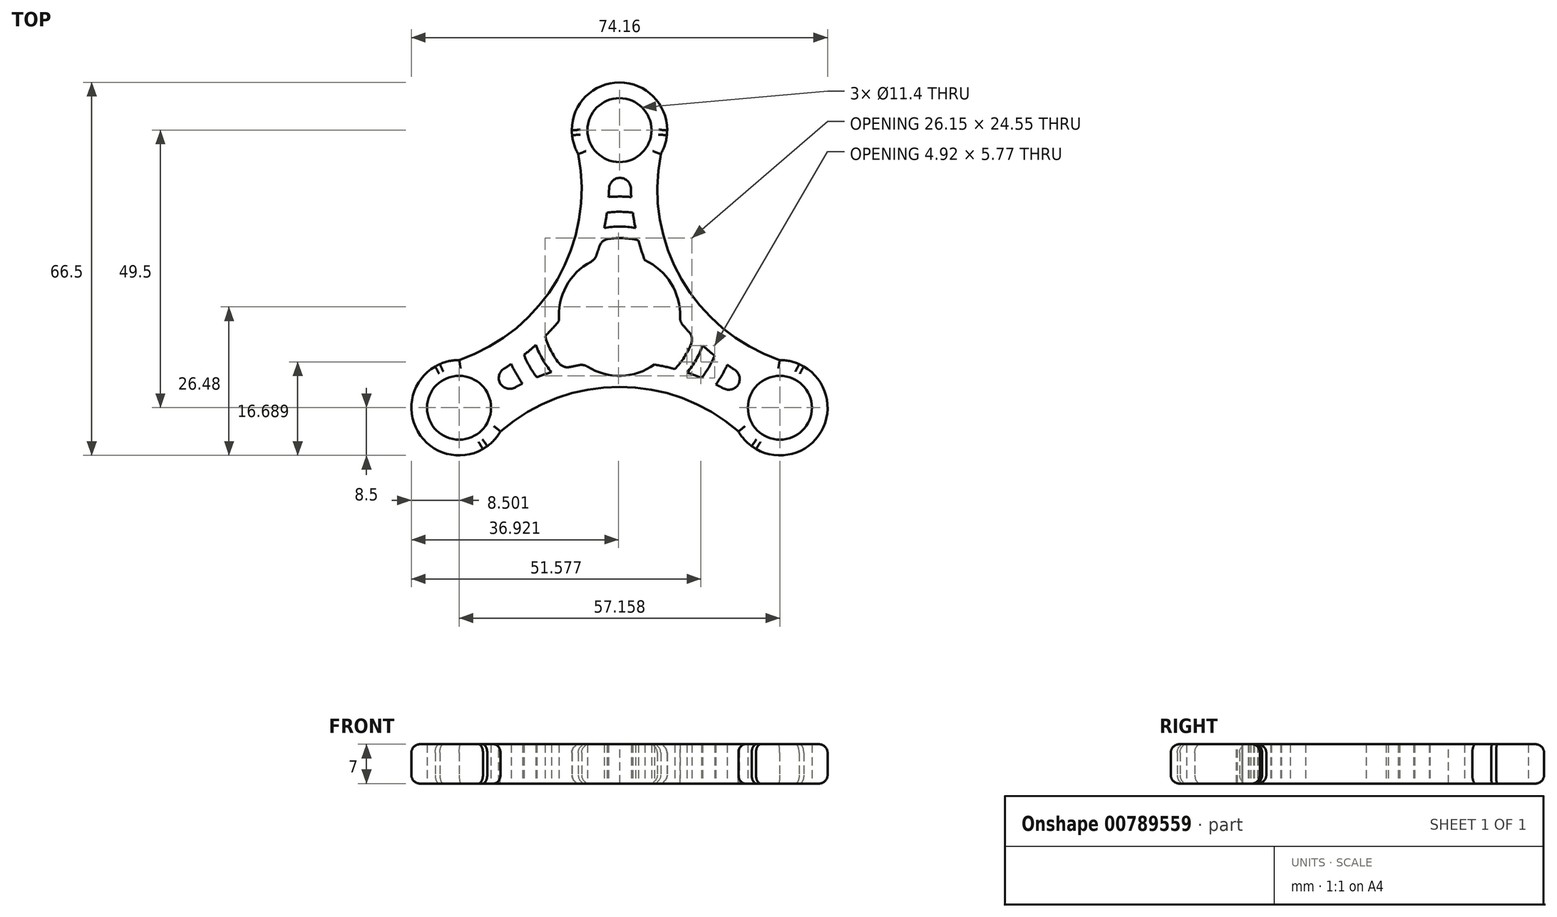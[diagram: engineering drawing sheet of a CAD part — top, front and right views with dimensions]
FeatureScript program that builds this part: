
annotation { "Feature Type Name" : "Feature", "Feature Type Description" : "" }
export const myFeature = defineFeature(function(context is Context, id is Id, definition is map)
    precondition{}
    {
        {
            var Q0;
            Q0=qCreatedBy(makeId("Top.planeOp"),FACE);
            var sketch = newSketch(context, id + "F0", { "sketchPlane" : qUnion([Q0])});
            skCircle(sketch, "E0", {"center": v(0, 0) * mm, "radius": 10.8 * mm});
            skCircle(sketch, "E1", {"center": v(0, 33) * mm, "radius": 5.7 * mm});
            skArc(sketch, "E2", {"start": v(7.35, 28.73) * mm, "mid": v(0, 41.5) * mm, "end": v(-7.35, 28.73) * mm});
            skCircle(sketch, "E3.1.0", {"center": v(-28.58, -16.5) * mm, "radius": 5.7 * mm});
            skArc(sketch, "E3.1.1", {"start": v(-28.55, -8) * mm, "mid": v(-35.94, -20.75) * mm, "end": v(-21.2, -20.73) * mm});
            skCircle(sketch, "E3.2.0", {"center": v(28.58, -16.5) * mm, "radius": 5.7 * mm});
            skArc(sketch, "E3.2.1", {"start": v(22.31, -10.76) * mm, "mid": v(21.17, -12.34) * mm, "end": v(20.41, -14.14) * mm});
            skLineSegment(sketch, "E4", {"start": v(0, 0) * mm, "end": v(28.58, -16.5) * mm, "construction": true});
            skLineSegment(sketch, "E5", {"start": v(28.58, -16.5) * mm, "end": v(38.1, 0) * mm, "construction": true});
            skArc(sketch, "E6", {"start": v(8.5, 33) * mm, "mid": v(8.47, 32.54) * mm, "end": v(8.45, 32.09) * mm});
            skArc(sketch, "E7.1.0", {"start": v(-32.83, -9.14) * mm, "mid": v(-32.42, -8.93) * mm, "end": v(-32.01, -8.72) * mm});
            skArc(sketch, "E7.2.0", {"start": v(24.33, -23.86) * mm, "mid": v(23.95, -23.6) * mm, "end": v(23.56, -23.36) * mm});
            skArc(sketch, "E8", {"start": v(2.04, 24.75) * mm, "mid": v(2.03, 22.9) * mm, "end": v(2.1, 21.05) * mm});
            skArc(sketch, "E9.trimOffspring", {"start": v(10.74, -1.1) * mm, "mid": v(11.94, -2.5) * mm, "end": v(13.2, -3.85) * mm});
            skArc(sketch, "E10.trimOffspring", {"start": v(-6.32, -8.76) * mm, "mid": v(-8.14, -9.1) * mm, "end": v(-9.94, -9.5) * mm});
            skArc(sketch, "E11.trimOffspring", {"start": v(-4.43, 9.85) * mm, "mid": v(-3.8, 11.6) * mm, "end": v(-3.27, 13.36) * mm});
            skArc(sketch, "E12.trimOffspring", {"start": v(32.01, -8.72) * mm, "mid": v(32.42, -8.93) * mm, "end": v(32.83, -9.14) * mm});
            skArc(sketch, "E13.trimOffspring", {"start": v(-23.56, -23.36) * mm, "mid": v(-23.95, -23.6) * mm, "end": v(-24.33, -23.86) * mm});
            skArc(sketch, "E14.trimOffspring", {"start": v(-8.45, 32.09) * mm, "mid": v(-8.47, 32.54) * mm, "end": v(-8.5, 33) * mm});
            skArc(sketch, "E15", {"start": v(7.35, 28.73) * mm, "mid": v(11.06, 6.38) * mm, "end": v(28.55, -8) * mm});
            skArc(sketch, "E16.1.0", {"start": v(-28.55, -8) * mm, "mid": v(-11.06, 6.38) * mm, "end": v(-7.35, 28.73) * mm});
            skArc(sketch, "E16.2.0", {"start": v(21.2, -20.73) * mm, "mid": v(0, -12.77) * mm, "end": v(-21.2, -20.73) * mm});
            skPoint(sketch, "E17.orphan", {"position": v(-2.9, 33) * mm});
            skPoint(sketch, "E18.orphan", {"position": v(3.18, 33) * mm});
            skArc(sketch, "E19.trimOffspring", {"start": v(-1.84, 24.7) * mm, "mid": v(0.1, 24.5) * mm, "end": v(2.04, 24.75) * mm});
            skPoint(sketch, "E20.orphan", {"position": v(-8.5, 33) * mm});
            skArc(sketch, "E21.trimOffspring", {"start": v(20.41, -14.14) * mm, "mid": v(18.82, -13.2) * mm, "end": v(17.18, -12.35) * mm});
            skArc(sketch, "E22.trimOffspring", {"start": v(21.2, -20.73) * mm, "mid": v(35.94, -20.75) * mm, "end": v(28.55, -8) * mm});
            skPoint(sketch, "E23.orphan", {"position": v(24.33, -23.86) * mm});
            skArc(sketch, "E24.trimOffspring", {"start": v(-22.45, -10.6) * mm, "mid": v(-20.84, -9.7) * mm, "end": v(-19.28, -8.7) * mm});
            skArc(sketch, "E25.trimOffspring", {"start": v(-20.47, -13.94) * mm, "mid": v(-21.27, -12.16) * mm, "end": v(-22.45, -10.6) * mm});
            skPoint(sketch, "E26.orphan", {"position": v(-32.83, -9.14) * mm});
            skPoint(sketch, "E27.orphan", {"position": v(-24.33, -23.86) * mm});
            skArc(sketch, "E28", {"start": v(-19.28, -8.7) * mm, "mid": v(-18.36, -10.5) * mm, "end": v(-17.28, -12.2) * mm});
            skArc(sketch, "E29", {"start": v(-17.02, -7.08) * mm, "mid": v(-16, -9.15) * mm, "end": v(-14.73, -11.08) * mm});
            skArc(sketch, "E30", {"start": v(-13.24, -3.74) * mm, "mid": v(-11.94, -6.83) * mm, "end": v(-9.94, -9.5) * mm});
            skArc(sketch, "E31", {"start": v(-14.88, -5.3) * mm, "mid": v(-13.72, -7.84) * mm, "end": v(-12.12, -10.14) * mm});
            skArc(sketch, "E32.trimOffspring", {"start": v(9.86, -9.6) * mm, "mid": v(11.88, -6.93) * mm, "end": v(13.2, -3.85) * mm});
            skArc(sketch, "E33.trimOffspring", {"start": v(12.04, -10.24) * mm, "mid": v(13.65, -7.96) * mm, "end": v(14.84, -5.43) * mm});
            skArc(sketch, "E34.trimOffspring", {"start": v(14.64, -11.2) * mm, "mid": v(15.92, -9.28) * mm, "end": v(16.96, -7.22) * mm});
            skArc(sketch, "E35.trimOffspring", {"start": v(17.18, -12.35) * mm, "mid": v(18.28, -10.65) * mm, "end": v(19.21, -8.86) * mm});
            skArc(sketch, "E36.trimOffspring", {"start": v(-17.28, -12.2) * mm, "mid": v(-18.9, -13.04) * mm, "end": v(-20.47, -13.94) * mm});
            skArc(sketch, "E37.trimOffspring", {"start": v(-17.02, -7.08) * mm, "mid": v(-15.93, -6.21) * mm, "end": v(-14.88, -5.3) * mm});
            skArc(sketch, "E38.trimOffspring", {"start": v(-13.24, -3.74) * mm, "mid": v(-11.96, -2.4) * mm, "end": v(-10.75, -1) * mm});
            skArc(sketch, "E39.trimOffspring", {"start": v(-12.12, -10.14) * mm, "mid": v(-13.43, -10.58) * mm, "end": v(-14.73, -11.08) * mm});
            skArc(sketch, "E40.trimOffspring", {"start": v(2.1, 21.05) * mm, "mid": v(0.09, 21.16) * mm, "end": v(-1.93, 21.07) * mm});
            skArc(sketch, "E41.trimOffspring", {"start": v(2.38, 18.28) * mm, "mid": v(0.08, 18.43) * mm, "end": v(-2.23, 18.3) * mm});
            skArc(sketch, "E42.trimOffspring", {"start": v(2.85, 15.54) * mm, "mid": v(0.06, 15.8) * mm, "end": v(-2.72, 15.56) * mm});
            skArc(sketch, "E43.trimOffspring", {"start": v(3.38, 13.33) * mm, "mid": v(0.06, 13.75) * mm, "end": v(-3.27, 13.36) * mm});
            skArc(sketch, "E44.trimOffspring", {"start": v(14.84, -5.43) * mm, "mid": v(15.88, -6.34) * mm, "end": v(16.96, -7.22) * mm});
            skArc(sketch, "E45.trimOffspring", {"start": v(9.86, -9.6) * mm, "mid": v(8.06, -9.16) * mm, "end": v(6.25, -8.81) * mm});
            skArc(sketch, "E46.trimOffspring", {"start": v(14.64, -11.2) * mm, "mid": v(13.35, -10.7) * mm, "end": v(12.04, -10.24) * mm});
            skArc(sketch, "E47.trimOffspring", {"start": v(19.21, -8.86) * mm, "mid": v(20.74, -9.85) * mm, "end": v(22.31, -10.76) * mm});
            skArc(sketch, "E48.trimOffspring", {"start": v(3.38, 13.33) * mm, "mid": v(3.9, 11.56) * mm, "end": v(4.5, 9.81) * mm});
            skArc(sketch, "E49.trimOffspring", {"start": v(-2.72, 15.56) * mm, "mid": v(-2.45, 16.93) * mm, "end": v(-2.23, 18.3) * mm});
            skArc(sketch, "E50.trimOffspring", {"start": v(-1.93, 21.07) * mm, "mid": v(-1.84, 22.88) * mm, "end": v(-1.84, 24.7) * mm});
            skArc(sketch, "E51.trimOffspring", {"start": v(2.38, 18.28) * mm, "mid": v(2.59, 16.9) * mm, "end": v(2.85, 15.54) * mm});
            skSolve(sketch);
        }
        {
            var Q0;
            Q0=makeQuery(id+"F0.imprint","IMPRINT",FACE,{"disambiguationData":[TD([[makeQuery(id+"F0.imprint","IMPRINT",EDGE,{"derivedFrom":sQuery(id+"F0.wireOp",EDGE,"E1")}),-1.0]])]});
            extrude(context, id + "F1", {"entities" : qUnion([Q0]), "depth" : 7 * mm, "offsetDistance" : 25 * mm});
        }
        {
            var Q0;
            Q0=makeQuery(id+"F1.opExtrude","SWEPT_EDGE",EDGE,{"disambiguationData":[OSD([sQuery(id+"F0.wireOp",EDGE,"E11.trimOffspring"),sQuery(id+"F0.wireOp",EDGE,"E19.trimOffspring")])]});
            var Q1;
            Q1=makeQuery(id+"F1.opExtrude","SWEPT_EDGE",EDGE,{"disambiguationData":[OSD([sQuery(id+"F0.wireOp",EDGE,"E8"),sQuery(id+"F0.wireOp",EDGE,"E19.trimOffspring")])]});
            var Q2;
            Q2=makeQuery(id+"F1.opExtrude","SWEPT_EDGE",EDGE,{"disambiguationData":[OSD([sQuery(id+"F0.wireOp",EDGE,"E3.2.1"),sQuery(id+"F0.wireOp",EDGE,"E9.trimOffspring")])]});
            var Q3;
            Q3=makeQuery(id+"F1.opExtrude","SWEPT_EDGE",EDGE,{"disambiguationData":[OSD([sQuery(id+"F0.wireOp",EDGE,"E3.2.1"),sQuery(id+"F0.wireOp",EDGE,"E21.trimOffspring")])]});
            var Q4;
            Q4=makeQuery(id+"F1.opExtrude","SWEPT_EDGE",EDGE,{"disambiguationData":[OSD([sQuery(id+"F0.wireOp",EDGE,"E10.trimOffspring"),sQuery(id+"F0.wireOp",EDGE,"E25.trimOffspring")])]});
            var Q5;
            Q5=makeQuery(id+"F1.opExtrude","SWEPT_EDGE",EDGE,{"disambiguationData":[OSD([sQuery(id+"F0.wireOp",EDGE,"E24.trimOffspring"),sQuery(id+"F0.wireOp",EDGE,"E25.trimOffspring")])]});
            fillet(context, id + "F2", {"entities" : qUnion([Q0, Q1, Q2, Q3, Q4, Q5]), "radius" : 2 * mm, "tangentPropagation" : true, "allowEdgeOverflow" : false});
        }
        {
            var Q0;
            Q0=makeQuery(id+"F1.opExtrude","CAP_EDGE",EDGE,{"disambiguationData":[OSD([sQuery(id+"F0.wireOp",EDGE,"E16.2.0")])],"isStart":false});
            var Q1;
            Q1=makeQuery(id+"F1.opExtrude","CAP_EDGE",EDGE,{"disambiguationData":[OSD([sQuery(id+"F0.wireOp",EDGE,"E15")])],"isStart":false});
            var Q2;
            Q2=makeQuery(id+"F1.opExtrude","CAP_EDGE",EDGE,{"disambiguationData":[OSD([sQuery(id+"F0.wireOp",EDGE,"E16.1.0")])],"isStart":false});
            var Q3;
            Q3=makeQuery(id+"F1.opExtrude","CAP_EDGE",EDGE,{"disambiguationData":[OSD([sQuery(id+"F0.wireOp",EDGE,"E16.2.0")])],"isStart":true});
            var Q4;
            Q4=makeQuery(id+"F1.opExtrude","CAP_EDGE",EDGE,{"disambiguationData":[OSD([sQuery(id+"F0.wireOp",EDGE,"E15")])],"isStart":true});
            var Q5;
            Q5=makeQuery(id+"F1.opExtrude","CAP_EDGE",EDGE,{"disambiguationData":[OSD([sQuery(id+"F0.wireOp",EDGE,"E16.1.0")])],"isStart":true});
            var Q6;
            {var subQ0=sQuery(id+"F0.wireOp",EDGE,"E3.1.1");Q6=makeQuery(id+"F1.opExtrude","CAP_EDGE",EDGE,{"disambiguationData":[OSD([subQ0]),TDD([makeQuery(id+"F0.imprint","IMPRINT",EDGE,{"disambiguationData":[TD([[makeQuery(id+"F0.imprint","INTERSECT",VERTEX,{"disambiguationData":[OD(0.0)],"derivedFrom":[subQ0,sQuery(id+"F0.wireOp",EDGE,"E7.1.0")]}),-1.0]])],"derivedFrom":subQ0})])],"isStart":true});}
            var Q7;
            {var subQ0=sQuery(id+"F0.wireOp",EDGE,"E3.1.1");Q7=makeQuery(id+"F1.opExtrude","CAP_EDGE",EDGE,{"disambiguationData":[OSD([subQ0]),TDD([makeQuery(id+"F0.imprint","IMPRINT",EDGE,{"disambiguationData":[TD([[makeQuery(id+"F0.imprint","INTERSECT",VERTEX,{"derivedFrom":[subQ0,sQuery(id+"F0.wireOp",EDGE,"E16.1.0")]}),-1.0]])],"derivedFrom":subQ0})])],"isStart":true});}
            var Q8;
            Q8=makeQuery(id+"F1.opExtrude","CAP_EDGE",EDGE,{"disambiguationData":[OSD([sQuery(id+"F0.wireOp",EDGE,"E7.1.0")])],"isStart":true});
            var Q9;
            {var subQ0=sQuery(id+"F0.wireOp",EDGE,"E3.1.1");Q9=makeQuery(id+"F1.opExtrude","CAP_EDGE",EDGE,{"disambiguationData":[OSD([subQ0]),TDD([makeQuery(id+"F0.imprint","IMPRINT",EDGE,{"disambiguationData":[TD([[makeQuery(id+"F0.imprint","INTERSECT",VERTEX,{"derivedFrom":[subQ0,sQuery(id+"F0.wireOp",EDGE,"E16.2.0")]}),1.0]])],"derivedFrom":subQ0})])],"isStart":true});}
            var Q10;
            Q10=makeQuery(id+"F1.opExtrude","CAP_EDGE",EDGE,{"disambiguationData":[OSD([sQuery(id+"F0.wireOp",EDGE,"E13.trimOffspring")])],"isStart":true});
            var Q11;
            {var subQ0=sQuery(id+"F0.wireOp",EDGE,"E22.trimOffspring");Q11=makeQuery(id+"F1.opExtrude","CAP_EDGE",EDGE,{"disambiguationData":[OSD([subQ0]),TDD([makeQuery(id+"F0.imprint","IMPRINT",EDGE,{"disambiguationData":[TD([[makeQuery(id+"F0.imprint","INTERSECT",VERTEX,{"disambiguationData":[OD(0.0)],"derivedFrom":[sQuery(id+"F0.wireOp",EDGE,"E12.trimOffspring"),subQ0]}),-1.0]])],"derivedFrom":subQ0})])],"isStart":true});}
            var Q12;
            Q12=makeQuery(id+"F1.opExtrude","CAP_EDGE",EDGE,{"disambiguationData":[OSD([sQuery(id+"F0.wireOp",EDGE,"E12.trimOffspring")])],"isStart":true});
            var Q13;
            {var subQ0=sQuery(id+"F0.wireOp",EDGE,"E22.trimOffspring");Q13=makeQuery(id+"F1.opExtrude","CAP_EDGE",EDGE,{"disambiguationData":[OSD([subQ0]),TDD([makeQuery(id+"F0.imprint","IMPRINT",EDGE,{"disambiguationData":[TD([[makeQuery(id+"F0.imprint","INTERSECT",VERTEX,{"disambiguationData":[OD(0.0)],"derivedFrom":[sQuery(id+"F0.wireOp",EDGE,"E7.2.0"),subQ0]}),-1.0]])],"derivedFrom":subQ0})])],"isStart":true});}
            var Q14;
            Q14=makeQuery(id+"F1.opExtrude","CAP_EDGE",EDGE,{"disambiguationData":[OSD([sQuery(id+"F0.wireOp",EDGE,"E7.2.0")])],"isStart":true});
            var Q15;
            {var subQ0=sQuery(id+"F0.wireOp",EDGE,"E22.trimOffspring");Q15=makeQuery(id+"F1.opExtrude","CAP_EDGE",EDGE,{"disambiguationData":[OSD([subQ0]),TDD([makeQuery(id+"F0.imprint","IMPRINT",EDGE,{"disambiguationData":[TD([[makeQuery(id+"F0.imprint","INTERSECT",VERTEX,{"disambiguationData":[OD(1.0)],"derivedFrom":[sQuery(id+"F0.wireOp",EDGE,"E7.2.0"),subQ0]}),1.0]])],"derivedFrom":subQ0})])],"isStart":true});}
            var Q16;
            {var subQ0=sQuery(id+"F0.wireOp",EDGE,"E2");Q16=makeQuery(id+"F1.opExtrude","CAP_EDGE",EDGE,{"disambiguationData":[OSD([subQ0]),TDD([makeQuery(id+"F0.imprint","IMPRINT",EDGE,{"disambiguationData":[TD([[makeQuery(id+"F0.imprint","INTERSECT",VERTEX,{"derivedFrom":[subQ0,sQuery(id+"F0.wireOp",EDGE,"E16.1.0")]}),1.0]])],"derivedFrom":subQ0})])],"isStart":true});}
            var Q17;
            Q17=makeQuery(id+"F1.opExtrude","CAP_EDGE",EDGE,{"disambiguationData":[OSD([sQuery(id+"F0.wireOp",EDGE,"E14.trimOffspring")])],"isStart":true});
            var Q18;
            {var subQ0=sQuery(id+"F0.wireOp",EDGE,"E2");Q18=makeQuery(id+"F1.opExtrude","CAP_EDGE",EDGE,{"disambiguationData":[OSD([subQ0]),TDD([makeQuery(id+"F0.imprint","IMPRINT",EDGE,{"disambiguationData":[TD([[makeQuery(id+"F0.imprint","INTERSECT",VERTEX,{"disambiguationData":[OD(0.0)],"derivedFrom":[subQ0,sQuery(id+"F0.wireOp",EDGE,"E6")]}),-1.0]])],"derivedFrom":subQ0})])],"isStart":true});}
            var Q19;
            {var subQ0=sQuery(id+"F0.wireOp",EDGE,"E2");Q19=makeQuery(id+"F1.opExtrude","CAP_EDGE",EDGE,{"disambiguationData":[OSD([subQ0]),TDD([makeQuery(id+"F0.imprint","IMPRINT",EDGE,{"disambiguationData":[TD([[makeQuery(id+"F0.imprint","INTERSECT",VERTEX,{"derivedFrom":[subQ0,sQuery(id+"F0.wireOp",EDGE,"E15")]}),-1.0]])],"derivedFrom":subQ0})])],"isStart":true});}
            var Q20;
            Q20=makeQuery(id+"F1.opExtrude","CAP_EDGE",EDGE,{"disambiguationData":[OSD([sQuery(id+"F0.wireOp",EDGE,"E6")])],"isStart":true});
            var Q21;
            {var subQ0=sQuery(id+"F0.wireOp",EDGE,"E2");Q21=makeQuery(id+"F1.opExtrude","CAP_EDGE",EDGE,{"disambiguationData":[OSD([subQ0]),TDD([makeQuery(id+"F0.imprint","IMPRINT",EDGE,{"disambiguationData":[TD([[makeQuery(id+"F0.imprint","INTERSECT",VERTEX,{"derivedFrom":[subQ0,sQuery(id+"F0.wireOp",EDGE,"E16.1.0")]}),1.0]])],"derivedFrom":subQ0})])],"isStart":false});}
            var Q22;
            Q22=makeQuery(id+"F1.opExtrude","CAP_EDGE",EDGE,{"disambiguationData":[OSD([sQuery(id+"F0.wireOp",EDGE,"E14.trimOffspring")])],"isStart":false});
            var Q23;
            {var subQ0=sQuery(id+"F0.wireOp",EDGE,"E2");Q23=makeQuery(id+"F1.opExtrude","CAP_EDGE",EDGE,{"disambiguationData":[OSD([subQ0]),TDD([makeQuery(id+"F0.imprint","IMPRINT",EDGE,{"disambiguationData":[TD([[makeQuery(id+"F0.imprint","INTERSECT",VERTEX,{"disambiguationData":[OD(0.0)],"derivedFrom":[subQ0,sQuery(id+"F0.wireOp",EDGE,"E6")]}),-1.0]])],"derivedFrom":subQ0})])],"isStart":false});}
            var Q24;
            {var subQ0=sQuery(id+"F0.wireOp",EDGE,"E2");Q24=makeQuery(id+"F1.opExtrude","CAP_EDGE",EDGE,{"disambiguationData":[OSD([subQ0]),TDD([makeQuery(id+"F0.imprint","IMPRINT",EDGE,{"disambiguationData":[TD([[makeQuery(id+"F0.imprint","INTERSECT",VERTEX,{"derivedFrom":[subQ0,sQuery(id+"F0.wireOp",EDGE,"E15")]}),-1.0]])],"derivedFrom":subQ0})])],"isStart":false});}
            var Q25;
            Q25=makeQuery(id+"F1.opExtrude","CAP_EDGE",EDGE,{"disambiguationData":[OSD([sQuery(id+"F0.wireOp",EDGE,"E6")])],"isStart":false});
            var Q26;
            {var subQ0=sQuery(id+"F0.wireOp",EDGE,"E22.trimOffspring");Q26=makeQuery(id+"F1.opExtrude","CAP_EDGE",EDGE,{"disambiguationData":[OSD([subQ0]),TDD([makeQuery(id+"F0.imprint","IMPRINT",EDGE,{"disambiguationData":[TD([[makeQuery(id+"F0.imprint","INTERSECT",VERTEX,{"disambiguationData":[OD(0.0)],"derivedFrom":[sQuery(id+"F0.wireOp",EDGE,"E12.trimOffspring"),subQ0]}),-1.0]])],"derivedFrom":subQ0})])],"isStart":false});}
            var Q27;
            Q27=makeQuery(id+"F1.opExtrude","CAP_EDGE",EDGE,{"disambiguationData":[OSD([sQuery(id+"F0.wireOp",EDGE,"E12.trimOffspring")])],"isStart":false});
            var Q28;
            {var subQ0=sQuery(id+"F0.wireOp",EDGE,"E22.trimOffspring");Q28=makeQuery(id+"F1.opExtrude","CAP_EDGE",EDGE,{"disambiguationData":[OSD([subQ0]),TDD([makeQuery(id+"F0.imprint","IMPRINT",EDGE,{"disambiguationData":[TD([[makeQuery(id+"F0.imprint","INTERSECT",VERTEX,{"disambiguationData":[OD(0.0)],"derivedFrom":[sQuery(id+"F0.wireOp",EDGE,"E7.2.0"),subQ0]}),-1.0]])],"derivedFrom":subQ0})])],"isStart":false});}
            var Q29;
            Q29=makeQuery(id+"F1.opExtrude","CAP_EDGE",EDGE,{"disambiguationData":[OSD([sQuery(id+"F0.wireOp",EDGE,"E7.2.0")])],"isStart":false});
            var Q30;
            {var subQ0=sQuery(id+"F0.wireOp",EDGE,"E22.trimOffspring");Q30=makeQuery(id+"F1.opExtrude","CAP_EDGE",EDGE,{"disambiguationData":[OSD([subQ0]),TDD([makeQuery(id+"F0.imprint","IMPRINT",EDGE,{"disambiguationData":[TD([[makeQuery(id+"F0.imprint","INTERSECT",VERTEX,{"disambiguationData":[OD(1.0)],"derivedFrom":[sQuery(id+"F0.wireOp",EDGE,"E7.2.0"),subQ0]}),1.0]])],"derivedFrom":subQ0})])],"isStart":false});}
            var Q31;
            {var subQ0=sQuery(id+"F0.wireOp",EDGE,"E3.1.1");Q31=makeQuery(id+"F1.opExtrude","CAP_EDGE",EDGE,{"disambiguationData":[OSD([subQ0]),TDD([makeQuery(id+"F0.imprint","IMPRINT",EDGE,{"disambiguationData":[TD([[makeQuery(id+"F0.imprint","INTERSECT",VERTEX,{"derivedFrom":[subQ0,sQuery(id+"F0.wireOp",EDGE,"E16.2.0")]}),1.0]])],"derivedFrom":subQ0})])],"isStart":false});}
            var Q32;
            Q32=makeQuery(id+"F1.opExtrude","CAP_EDGE",EDGE,{"disambiguationData":[OSD([sQuery(id+"F0.wireOp",EDGE,"E13.trimOffspring")])],"isStart":false});
            var Q33;
            {var subQ0=sQuery(id+"F0.wireOp",EDGE,"E3.1.1");Q33=makeQuery(id+"F1.opExtrude","CAP_EDGE",EDGE,{"disambiguationData":[OSD([subQ0]),TDD([makeQuery(id+"F0.imprint","IMPRINT",EDGE,{"disambiguationData":[TD([[makeQuery(id+"F0.imprint","INTERSECT",VERTEX,{"disambiguationData":[OD(0.0)],"derivedFrom":[subQ0,sQuery(id+"F0.wireOp",EDGE,"E7.1.0")]}),-1.0]])],"derivedFrom":subQ0})])],"isStart":false});}
            var Q34;
            {var subQ0=sQuery(id+"F0.wireOp",EDGE,"E3.1.1");Q34=makeQuery(id+"F1.opExtrude","CAP_EDGE",EDGE,{"disambiguationData":[OSD([subQ0]),TDD([makeQuery(id+"F0.imprint","IMPRINT",EDGE,{"disambiguationData":[TD([[makeQuery(id+"F0.imprint","INTERSECT",VERTEX,{"derivedFrom":[subQ0,sQuery(id+"F0.wireOp",EDGE,"E16.1.0")]}),-1.0]])],"derivedFrom":subQ0})])],"isStart":false});}
            var Q35;
            Q35=makeQuery(id+"F1.opExtrude","CAP_EDGE",EDGE,{"disambiguationData":[OSD([sQuery(id+"F0.wireOp",EDGE,"E7.1.0")])],"isStart":false});
            fillet(context, id + "F3", {"entities" : qUnion([Q0, Q1, Q2, Q3, Q4, Q5, Q6, Q7, Q8, Q9, Q10, Q11, Q12, Q13, Q14, Q15, Q16, Q17, Q18, Q19, Q20, Q21, Q22, Q23, Q24, Q25, Q26, Q27, Q28, Q29, Q30, Q31, Q32, Q33, Q34, Q35]), "radius" : 1.5 * mm, "tangentPropagation" : true, "allowEdgeOverflow" : false});
        }
    });
